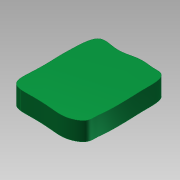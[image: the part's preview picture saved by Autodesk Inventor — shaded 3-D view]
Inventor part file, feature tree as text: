
AUTODESK INVENTOR PART (.ipt)
format: ipt  version: 2011 (Build 150239000, 239)  size: 90,624 bytes
history: native  units: mm
features: other x1, extrude x1, sketch x1
ambient origin geometry x8: Origin, YZ Plane, XZ Plane, XY Plane, X Axis, Y Axis, Z Axis, Center Point
feature tree (3):
  other  "РабПлоскость3"
  extrude  "Выдавливание4"  Depth=1.5mm TaperAngle=0.0deg
  sketch  "Эскиз4"
